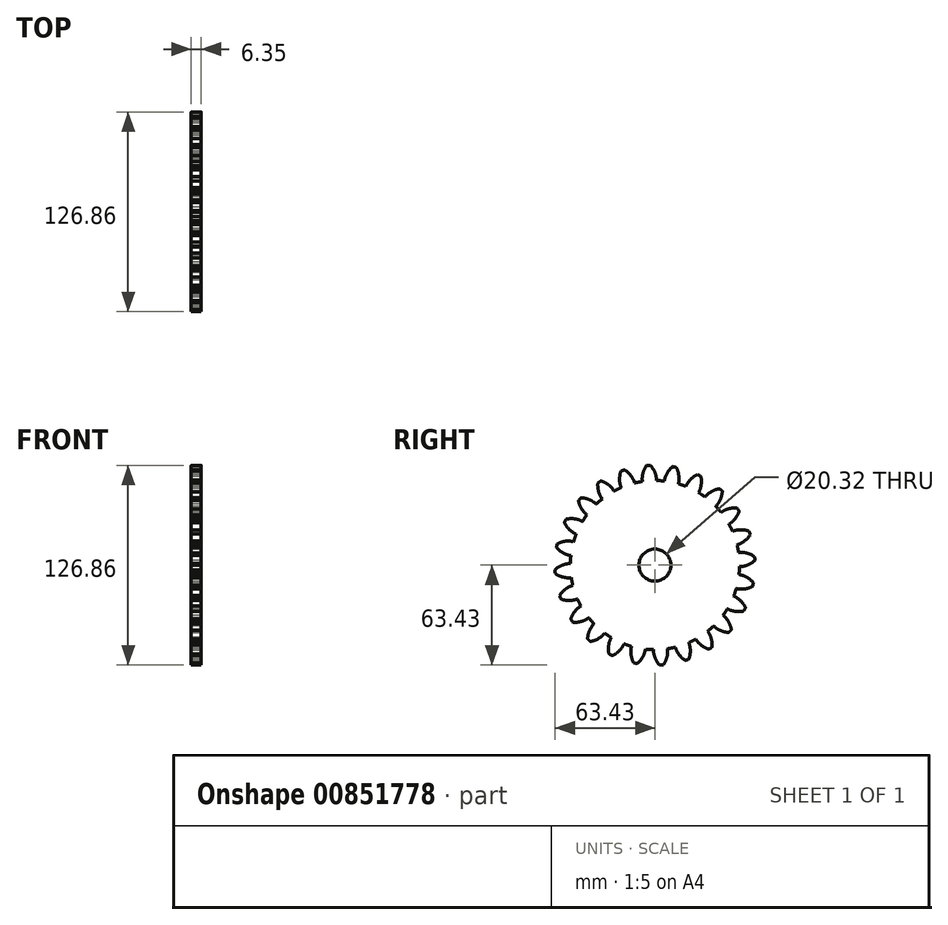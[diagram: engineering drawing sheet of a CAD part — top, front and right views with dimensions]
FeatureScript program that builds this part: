
annotation { "Feature Type Name" : "Feature", "Feature Type Description" : "" }
export const myFeature = defineFeature(function(context is Context, id is Id, definition is map)
    precondition{}
    {
        {
            var Q0;
            Q0=qCreatedBy(makeId("Right.planeOp"),FACE);
            var sketch = newSketch(context, id + "F0", { "sketchPlane" : qUnion([Q0])});
            skCircle(sketch, "E0", {"center": v(0, 0) * mm, "radius": 53.72 * mm});
            skCircle(sketch, "E1", {"center": v(0, 0) * mm, "radius": 58.67 * mm, "construction": true});
            skCircle(sketch, "E2", {"center": v(0, 0) * mm, "radius": 63.5 * mm, "construction": true});
            skLineSegment(sketch, "E3", {"start": v(0, 0) * mm, "end": v(0, 92.35) * mm, "construction": true});
            skLineSegment(sketch, "E4", {"start": v(0, 0) * mm, "end": v(-6.09, 92.87) * mm, "construction": true});
            skLineSegment(sketch, "E5", {"start": v(0, 58.67) * mm, "end": v(-70.37, 58.67) * mm, "construction": true});
            skLineSegment(sketch, "E6", {"start": v(0, 58.67) * mm, "end": v(-73.5, 31.92) * mm, "construction": true});
            skCircle(sketch, "E7", {"center": v(0, 58.67) * mm, "radius": 14.6 * mm, "construction": true});
            skCircle(sketch, "E8", {"center": v(0, 0) * mm, "radius": 55.14 * mm, "construction": true});
            skCircle(sketch, "E9", {"center": v(-13.62, 53.43) * mm, "radius": 14.6 * mm, "construction": true});
            skArc(sketch, "E10", {"start": v(0, 58.67) * mm, "mid": v(-1.24, 61.2) * mm, "end": v(-2.94, 63.43) * mm});
            skArc(sketch, "E11", {"start": v(0.99, 53.71) * mm, "mid": v(0.74, 56.24) * mm, "end": v(0, 58.67) * mm});
            skArc(sketch, "E12.MirrorCS", {"start": v(-7.66, 58.17) * mm, "mid": v(-6.75, 60.83) * mm, "end": v(-5.36, 63.27) * mm});
            skArc(sketch, "E13.MirrorCS", {"start": v(-7.99, 53.12) * mm, "mid": v(-8.07, 55.66) * mm, "end": v(-7.66, 58.17) * mm});
            skArc(sketch, "E14", {"start": v(-2.94, 63.43) * mm, "mid": v(-4.15, 63.39) * mm, "end": v(-5.36, 63.27) * mm});
            skSolve(sketch);
        }
        {
            var Q0;
            {var subQ0=sQuery(id+"F0.wireOp",EDGE,"E0");var subQ1=makeQuery(id+"F0.imprint","INTERSECT",VERTEX,{"derivedFrom":[subQ0,sQuery(id+"F0.wireOp",EDGE,"E11")]});Q0=makeQuery(id+"F0.imprint","IMPRINT",FACE,{"disambiguationData":[TD([[makeQuery(id+"F0.imprint","IMPRINT",EDGE,{"disambiguationData":[TD([[subQ1,-1.0]])],"derivedFrom":subQ0}),1.0]])]});}
            var Q1;
            Q1=makeQuery(id+"F0.imprint","IMPRINT",FACE,{"disambiguationData":[TD([[makeQuery(id+"F0.imprint","IMPRINT",EDGE,{"derivedFrom":sQuery(id+"F0.wireOp",EDGE,"E10")}),1.0]])]});
            extrude(context, id + "F1", {"entities" : qUnion([Q0, Q1]), "depth" : 6.35 * mm, "offsetDistance" : 25.4 * mm});
        }
        {
            var Q0;
            Q0=makeQuery(id+"F1.opExtrude","SWEPT_BODY",BODY,{"disambiguationData":[OSD([sQuery(id+"F0.wireOp",EDGE,"E0"),sQuery(id+"F0.wireOp",EDGE,"E10"),sQuery(id+"F0.wireOp",EDGE,"E11"),sQuery(id+"F0.wireOp",EDGE,"E12.MirrorCS"),sQuery(id+"F0.wireOp",EDGE,"E13.MirrorCS"),sQuery(id+"F0.wireOp",EDGE,"E14")])]});
            var Q1;
            Q1=makeQuery(id+"F1.opExtrude","SWEPT_FACE",FACE,{"disambiguationData":[OSD([sQuery(id+"F0.wireOp",EDGE,"E0")])]});
            circularPattern(context, id + "F2", {"operationType" : NewBodyOperationType.ADD, "entities" : qUnion([Q0]), "axis" : qUnion([Q1]), "angle" : 360 * degree, "instanceCount" : 24, "equalSpace" : true});
        }
        {
            var Q0;
            {var subQ0=makeQuery(id+"F1.opExtrude","CAP_FACE",FACE,{"disambiguationData":[OSD([sQuery(id+"F0.wireOp",EDGE,"E0"),sQuery(id+"F0.wireOp",EDGE,"E10"),sQuery(id+"F0.wireOp",EDGE,"E11"),sQuery(id+"F0.wireOp",EDGE,"E12.MirrorCS"),sQuery(id+"F0.wireOp",EDGE,"E13.MirrorCS"),sQuery(id+"F0.wireOp",EDGE,"E14")])],"isStart":false});Q0=makeQuery(id+"F2.boolean.opBoolean","MERGE",FACE,{"derivedFrom":[subQ0,makeQuery(id+"F2.opPattern","COPY",FACE,{"derivedFrom":subQ0,"instanceName":"1"}),makeQuery(id+"F2.opPattern","COPY",FACE,{"derivedFrom":subQ0,"instanceName":"2"}),makeQuery(id+"F2.opPattern","COPY",FACE,{"derivedFrom":subQ0,"instanceName":"3"}),makeQuery(id+"F2.opPattern","COPY",FACE,{"derivedFrom":subQ0,"instanceName":"4"}),makeQuery(id+"F2.opPattern","COPY",FACE,{"derivedFrom":subQ0,"instanceName":"5"}),makeQuery(id+"F2.opPattern","COPY",FACE,{"derivedFrom":subQ0,"instanceName":"6"}),makeQuery(id+"F2.opPattern","COPY",FACE,{"derivedFrom":subQ0,"instanceName":"7"}),makeQuery(id+"F2.opPattern","COPY",FACE,{"derivedFrom":subQ0,"instanceName":"8"}),makeQuery(id+"F2.opPattern","COPY",FACE,{"derivedFrom":subQ0,"instanceName":"9"}),makeQuery(id+"F2.opPattern","COPY",FACE,{"derivedFrom":subQ0,"instanceName":"10"}),makeQuery(id+"F2.opPattern","COPY",FACE,{"derivedFrom":subQ0,"instanceName":"11"}),makeQuery(id+"F2.opPattern","COPY",FACE,{"derivedFrom":subQ0,"instanceName":"12"}),makeQuery(id+"F2.opPattern","COPY",FACE,{"derivedFrom":subQ0,"instanceName":"13"}),makeQuery(id+"F2.opPattern","COPY",FACE,{"derivedFrom":subQ0,"instanceName":"14"}),makeQuery(id+"F2.opPattern","COPY",FACE,{"derivedFrom":subQ0,"instanceName":"15"}),makeQuery(id+"F2.opPattern","COPY",FACE,{"derivedFrom":subQ0,"instanceName":"16"}),makeQuery(id+"F2.opPattern","COPY",FACE,{"derivedFrom":subQ0,"instanceName":"17"}),makeQuery(id+"F2.opPattern","COPY",FACE,{"derivedFrom":subQ0,"instanceName":"18"}),makeQuery(id+"F2.opPattern","COPY",FACE,{"derivedFrom":subQ0,"instanceName":"19"}),makeQuery(id+"F2.opPattern","COPY",FACE,{"derivedFrom":subQ0,"instanceName":"20"}),makeQuery(id+"F2.opPattern","COPY",FACE,{"derivedFrom":subQ0,"instanceName":"21"}),makeQuery(id+"F2.opPattern","COPY",FACE,{"derivedFrom":subQ0,"instanceName":"22"}),makeQuery(id+"F2.opPattern","COPY",FACE,{"derivedFrom":subQ0,"instanceName":"23"})]});}
            var sketch = newSketch(context, id + "F3", { "sketchPlane" : qUnion([Q0])});
            skCircle(sketch, "E15", {"center": v(0, 0) * mm, "radius": 10.16 * mm});
            skSolve(sketch);
        }
        {
            var Q0;
            Q0 = qSketchRegion(id + "F3", true);
            extrude(context, id + "F4", {"entities" : qUnion([Q0]), "operationType" : NewBodyOperationType.REMOVE, "oppositeDirection" : true, "depth" : 25.4 * mm, "offsetDistance" : 25.4 * mm});
        }
    });
